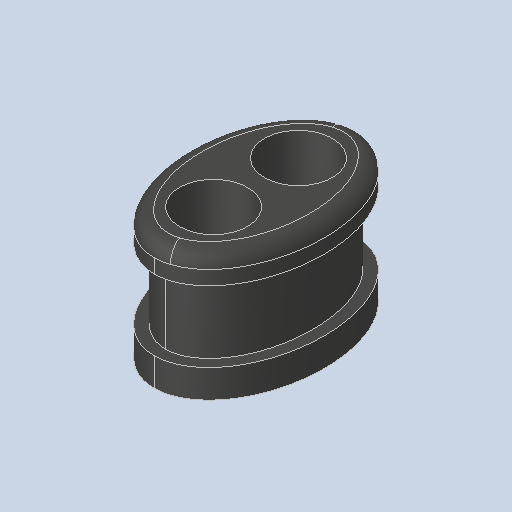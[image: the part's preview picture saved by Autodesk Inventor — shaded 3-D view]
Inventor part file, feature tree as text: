
AUTODESK INVENTOR PART (.ipt)
format: ipt  version: 2023.4 (Build 274418000, 418)  size: 173,056 bytes
history: native  units: in
note: dims shown in document units (in); Inventor stores cm internally (conversion verified against a paired STEP export)
features: fillet x1
ambient origin geometry x8: Origin, YZ Plane, XZ Plane, XY Plane, X Axis, Y Axis, Z Axis, Center Point
bodies: Solid1 (feature_tree)
feature tree (1):
  fillet  "Fillet1"  [1 undecoded]
note: 1 required parameter value undecoded (feature->parameter linkage not recoverable at this tier; creation-order binding heuristic only, values carry confidence <= 0.55)
